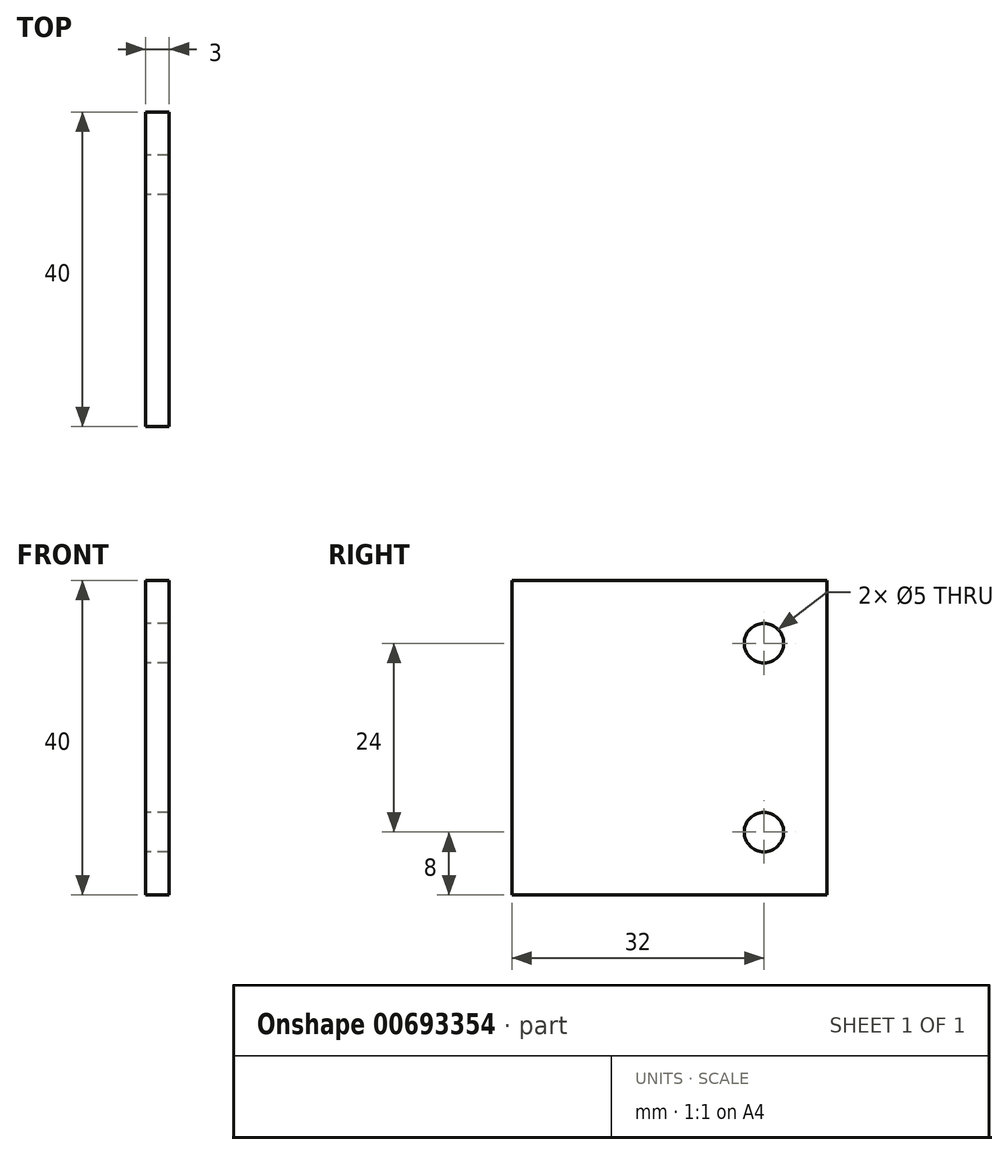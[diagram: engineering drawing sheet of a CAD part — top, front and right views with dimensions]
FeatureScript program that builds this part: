
annotation { "Feature Type Name" : "Feature", "Feature Type Description" : "" }
export const myFeature = defineFeature(function(context is Context, id is Id, definition is map)
    precondition{}
    {
        {
            var Q0;
            Q0=qCreatedBy(makeId("Right.planeOp"),FACE);
            var sketch = newSketch(context, id + "F0", { "sketchPlane" : qUnion([Q0])});
            skLineSegment(sketch, "E0.bottom", {"start": v(-40, 20) * mm, "end": v(0, 20) * mm});
            skLineSegment(sketch, "E0.top", {"start": v(-40, -20) * mm, "end": v(0, -20) * mm});
            skLineSegment(sketch, "E0.left", {"start": v(-40, 20) * mm, "end": v(-40, -20) * mm});
            skLineSegment(sketch, "E0.right", {"start": v(0, 20) * mm, "end": v(0, -20) * mm});
            skCircle(sketch, "E1", {"center": v(-8, 12) * mm, "radius": 2.5 * mm});
            skCircle(sketch, "E2", {"center": v(-8, -12) * mm, "radius": 2.5 * mm});
            skSolve(sketch);
        }
        {
            var Q0;
            Q0 = qSketchRegion(id + "F0", true);
            extrude(context, id + "F1", {"entities" : qUnion([Q0]), "depth" : 3 * mm, "offsetDistance" : 25 * mm});
        }
    });
